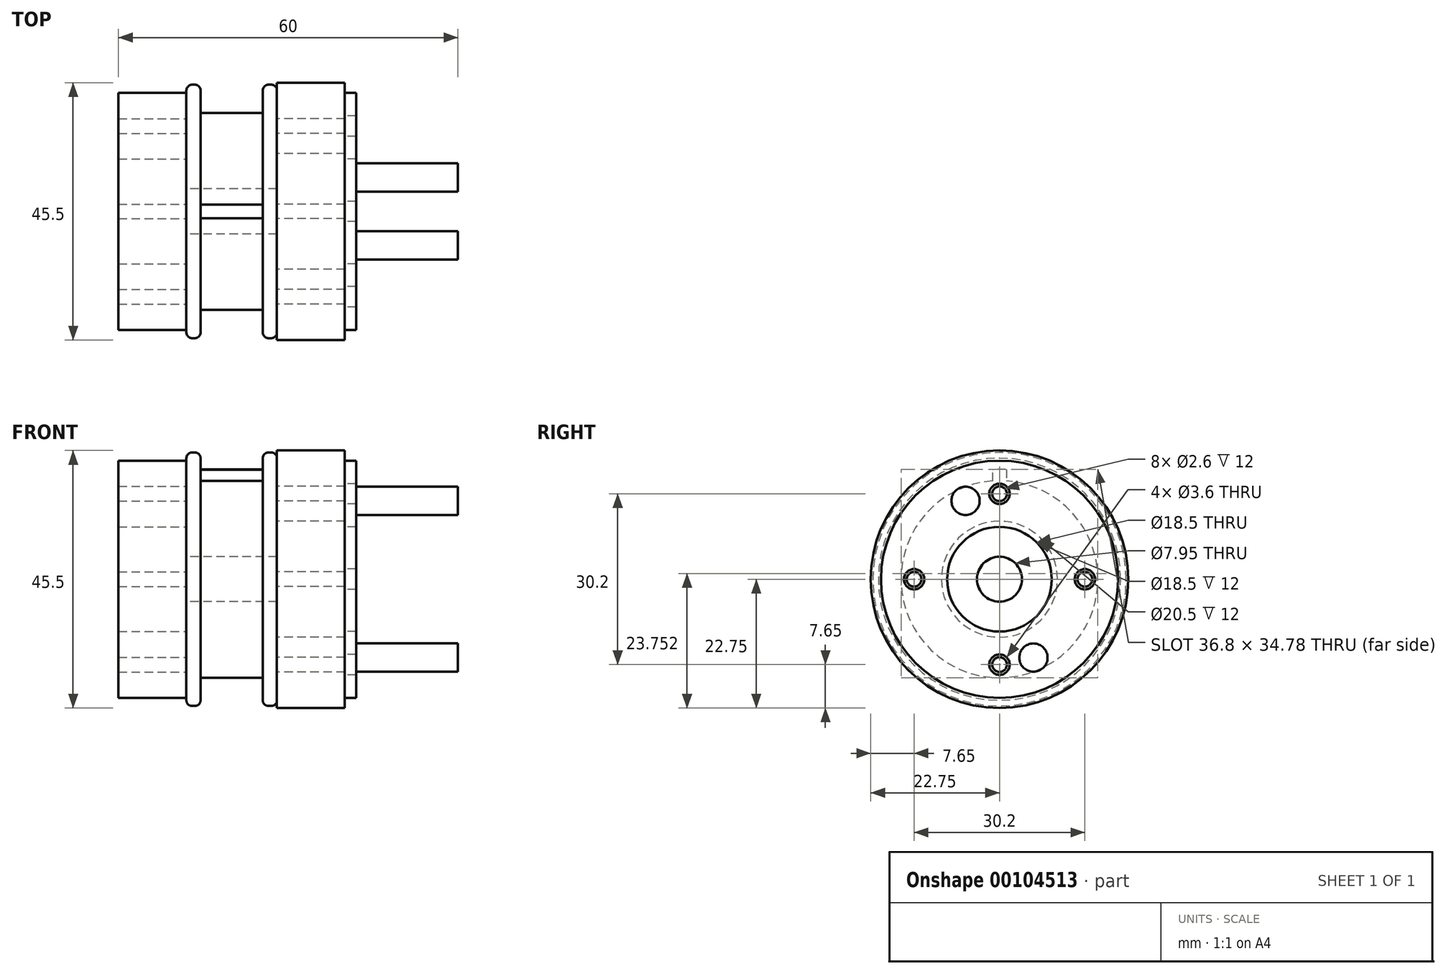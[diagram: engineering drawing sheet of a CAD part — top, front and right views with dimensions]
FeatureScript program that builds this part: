
annotation { "Feature Type Name" : "Feature", "Feature Type Description" : "" }
export const myFeature = defineFeature(function(context is Context, id is Id, definition is map)
    precondition{}
    {
        {
            var Q0;
            Q0=qCreatedBy(makeId("Right.planeOp"),FACE);
            var sketch = newSketch(context, id + "F0", { "sketchPlane" : qUnion([Q0])});
            skCircle(sketch, "E0", {"center": v(0, 0) * mm, "radius": 3.98 * mm});
            skCircle(sketch, "E1", {"center": v(0, 0) * mm, "radius": 14 * mm});
            skSolve(sketch);
        }
        {
            var Q0;
            Q0=makeQuery(id+"F0.imprint","IMPRINT",FACE,{"disambiguationData":[TD([[makeQuery(id+"F0.imprint","IMPRINT",EDGE,{"derivedFrom":sQuery(id+"F0.wireOp",EDGE,"E0")}),-1.0]])]});
            extrude(context, id + "F1", {"entities" : qUnion([Q0]), "endBound" : BoundingType.SYMMETRIC, "depth" : 16 * mm});
        }
        {
            var Q0;
            Q0=qCreatedBy(makeId("Right.planeOp"),FACE);
            var sketch = newSketch(context, id + "F2", { "sketchPlane" : qUnion([Q0])});
            skCircle(sketch, "E2", {"center": v(0, 0) * mm, "radius": 14 * mm});
            skCircle(sketch, "E3", {"center": v(0, 0) * mm, "radius": 17.4 * mm});
            skSolve(sketch);
        }
        {
            var Q0;
            Q0=makeQuery(id+"F2.imprint","IMPRINT",FACE,{"disambiguationData":[TD([[makeQuery(id+"F2.imprint","IMPRINT",EDGE,{"derivedFrom":sQuery(id+"F2.wireOp",EDGE,"E2")}),-1.0]])]});
            extrude(context, id + "F3", {"entities" : qUnion([Q0]), "operationType" : NewBodyOperationType.ADD, "endBound" : BoundingType.SYMMETRIC, "depth" : 16 * mm});
        }
        {
            var Q0;
            Q0=qCreatedBy(makeId("Front.planeOp"),FACE);
            var sketch = newSketch(context, id + "F4", { "sketchPlane" : qUnion([Q0])});
            skLineSegment(sketch, "E4", {"start": v(-27.37, 0) * mm, "end": v(29.66, 0) * mm});
            skLineSegment(sketch, "E5.bottom", {"start": v(-8, 22.4) * mm, "end": v(8, 22.4) * mm});
            skLineSegment(sketch, "E5.top", {"start": v(-8, 17.4) * mm, "end": v(8, 17.4) * mm});
            skLineSegment(sketch, "E5.left", {"start": v(-8, 22.4) * mm, "end": v(-8, 17.4) * mm});
            skLineSegment(sketch, "E5.right", {"start": v(8, 22.4) * mm, "end": v(8, 17.4) * mm});
            skLineSegment(sketch, "E6", {"start": v(-5.5, 22.4) * mm, "end": v(-5.5, 17.4) * mm});
            skLineSegment(sketch, "E7", {"start": v(5.5, 22.4) * mm, "end": v(5.5, 17.4) * mm});
            skSolve(sketch);
        }
        {
            var Q0;
            {var subQ0=sQuery(id+"F4.wireOp",EDGE,"E5.left");Q0=makeQuery(id+"F4.imprint","IMPRINT",FACE,{"disambiguationData":[TD([[makeQuery(id+"F4.imprint","IMPRINT",EDGE,{"derivedFrom":subQ0}),1.0]])]});}
            var Q1;
            {var subQ0=sQuery(id+"F4.wireOp",EDGE,"E5.right");Q1=makeQuery(id+"F4.imprint","IMPRINT",FACE,{"disambiguationData":[TD([[makeQuery(id+"F4.imprint","IMPRINT",EDGE,{"derivedFrom":subQ0}),-1.0]])]});}
            var Q2;
            Q2=sQuery(id+"F4.wireOp",EDGE,"E4");
            revolve(context, id + "F5", {"operationType" : NewBodyOperationType.ADD, "entities" : qUnion([Q0, Q1]), "axis" : qUnion([Q2]), "revolveType" : RevolveType.FULL});
        }
        {
            var Q0;
            {var subQ0=sQuery(id+"F4.wireOp",EDGE,"E6");Q0=makeQuery(id+"FOtlNRIKVtqWGdL_1.boolean.opBoolean","MERGE",FACE,{"derivedFrom":[makeQuery(id+"F5.opRevolve","SWEPT_FACE",FACE,{"disambiguationData":[OSD([subQ0])]}),makeQuery(id+"FOtlNRIKVtqWGdL_1.opRevolve","SWEPT_FACE",FACE,{"disambiguationData":[OSD([subQ0])]})]});}
            var sketch = newSketch(context, id + "F6", { "sketchPlane" : qUnion([Q0])});
            skArc(sketch, "E8", {"start": v(-1.2, 17.36) * mm, "mid": v(0, -17.4) * mm, "end": v(1.2, 17.36) * mm, "construction": true});
            skArc(sketch, "E9", {"start": v(1.2, 17.36) * mm, "mid": v(0, 17.4) * mm, "end": v(-1.2, 17.36) * mm});
            skPoint(sketch, "E10.visualSharp", {"position": v(-1.2, 19.37) * mm});
            skPoint(sketch, "E11.visualSharp", {"position": v(1.2, 19.37) * mm});
            skArc(sketch, "E12", {"start": v(-0.97, 19.38) * mm, "mid": v(0, -19.4) * mm, "end": v(0.98, 19.38) * mm});
            skArc(sketch, "E13", {"start": v(0.98, 19.38) * mm, "mid": v(-0.29, 19.4) * mm, "end": v(-1.55, 19.34) * mm});
            skLineSegment(sketch, "E14", {"start": v(-1.2, 17.36) * mm, "end": v(-1.2, 19.37) * mm});
            skLineSegment(sketch, "E15", {"start": v(1.2, 19.37) * mm, "end": v(1.2, 17.36) * mm});
            skSolve(sketch);
        }
        {
            var Q0;
            {var subQ0=sQuery(id+"F6.wireOp",EDGE,"E13");var subQ3=makeQuery(id+"F6.imprint","IMPRINT",VERTEX,{"derivedFrom":subQ0});Q0=makeQuery(id+"F6.imprint","IMPRINT",FACE,{"disambiguationData":[TD([[makeQuery(id+"F6.imprint","IMPRINT",EDGE,{"disambiguationData":[TD([[subQ3,1.0]])],"derivedFrom":subQ0}),1.0]])]});}
            var Q1;
            Q1=makeQuery(id+"F5.opRevolve","SWEPT_FACE",FACE,{"disambiguationData":[OSD([sQuery(id+"F4.wireOp",EDGE,"E7")])]});
            extrude(context, id + "F7", {"entities" : qUnion([Q0]), "operationType" : NewBodyOperationType.ADD, "endBound" : BoundingType.UP_TO_SURFACE, "endBoundEntityFace" : qUnion([Q1]), "depth" : 10 * mm});
        }
        {
            var Q0;
            Q0=makeQuery(id+"F5.opRevolve","SWEPT_EDGE",EDGE,{"disambiguationData":[OSD([sQuery(id+"F4.wireOp",EDGE,"E5.bottom"),sQuery(id+"F4.wireOp",EDGE,"E6")])]});
            var Q1;
            Q1=makeQuery(id+"F5.opRevolve","SWEPT_EDGE",EDGE,{"disambiguationData":[OSD([sQuery(id+"F4.wireOp",EDGE,"E5.bottom"),sQuery(id+"F4.wireOp",EDGE,"E7")])]});
            var Q2;
            Q2=makeQuery(id+"F5.opRevolve","SWEPT_EDGE",EDGE,{"disambiguationData":[OSD([sQuery(id+"F4.wireOp",EDGE,"E5.bottom"),sQuery(id+"F4.wireOp",EDGE,"E5.left")])]});
            var Q3;
            Q3=makeQuery(id+"F5.opRevolve","SWEPT_EDGE",EDGE,{"disambiguationData":[OSD([sQuery(id+"F4.wireOp",EDGE,"E5.bottom"),sQuery(id+"F4.wireOp",EDGE,"E5.right")])]});
            fillet(context, id + "F8", {"entities" : qUnion([Q0, Q1, Q2, Q3]), "radius" : 1 * mm, "tangentPropagation" : true, "allowEdgeOverflow" : false});
        }
        {
            var Q0;
            Q0=makeQuery(id+"F1.opExtrude","CAP_FACE",FACE,{"disambiguationData":[OSD([sQuery(id+"F0.wireOp",EDGE,"E0"),sQuery(id+"F0.wireOp",EDGE,"E1")])],"isStart":true});
            var sketch = newSketch(context, id + "F9", { "sketchPlane" : qUnion([Q0])});
            skCircle(sketch, "E16", {"center": v(0, 0) * mm, "radius": 9.25 * mm});
            skCircle(sketch, "E17", {"center": v(0, 0) * mm, "radius": 20.95 * mm});
            skCircle(sketch, "E18", {"center": v(0, 15.1) * mm, "radius": 1.3 * mm});
            skCircle(sketch, "E19", {"center": v(-15.1, 0) * mm, "radius": 1.3 * mm});
            skCircle(sketch, "E20", {"center": v(15.1, 0) * mm, "radius": 1.3 * mm});
            skCircle(sketch, "E21", {"center": v(0, -15.1) * mm, "radius": 1.3 * mm});
            skSolve(sketch);
        }
        {
            var Q0;
            Q0=makeQuery(id+"F9.imprint","IMPRINT",FACE,{"disambiguationData":[TD([[makeQuery(id+"F9.imprint","IMPRINT",EDGE,{"derivedFrom":sQuery(id+"F9.wireOp",EDGE,"E16")}),-1.0]])]});
            var Q1;
            Q1=makeQuery(id+"F9.imprint","IMPRINT",FACE,{"disambiguationData":[TD([[makeQuery(id+"F9.imprint","IMPRINT",EDGE,{"derivedFrom":sQuery(id+"F9.wireOp",EDGE,"E17")}),1.0]])]});
            extrude(context, id + "F10", {"entities" : qUnion([Q0, Q1]), "operationType" : NewBodyOperationType.ADD, "depth" : 12 * mm});
        }
        {
            var Q0;
            Q0=makeQuery(id+"F5.boolean.opBoolean","MERGE",FACE,{"derivedFrom":[makeQuery(id+"F3.boolean.opBoolean","MERGE",FACE,{"derivedFrom":[makeQuery(id+"F1.opExtrude","CAP_FACE",FACE,{"disambiguationData":[OSD([sQuery(id+"F0.wireOp",EDGE,"E0"),sQuery(id+"F0.wireOp",EDGE,"E1")])],"isStart":false}),makeQuery(id+"F3.opExtrude","CAP_FACE",FACE,{"disambiguationData":[OSD([sQuery(id+"F2.wireOp",EDGE,"E2"),sQuery(id+"F2.wireOp",EDGE,"E3")])],"isStart":false})]}),makeQuery(id+"F5.opRevolve","SWEPT_FACE",FACE,{"disambiguationData":[OSD([sQuery(id+"F4.wireOp",EDGE,"E5.right")])]})]});
            var sketch = newSketch(context, id + "F11", { "sketchPlane" : qUnion([Q0])});
            skCircle(sketch, "E22", {"center": v(0, 0) * mm, "radius": 22.75 * mm});
            skCircle(sketch, "E23", {"center": v(0, 0) * mm, "radius": 10.25 * mm});
            skCircle(sketch, "E24", {"center": v(0, 15.1) * mm, "radius": 1.3 * mm});
            skCircle(sketch, "E25", {"center": v(-15.1, 0) * mm, "radius": 1.3 * mm});
            skCircle(sketch, "E26", {"center": v(0, -15.1) * mm, "radius": 1.3 * mm});
            skCircle(sketch, "E27", {"center": v(15.1, 0) * mm, "radius": 1.3 * mm});
            skSolve(sketch);
        }
        {
            var Q0;
            Q0=makeQuery(id+"F11.imprint","IMPRINT",FACE,{"disambiguationData":[TD([[makeQuery(id+"F11.imprint","IMPRINT",EDGE,{"derivedFrom":sQuery(id+"F11.wireOp",EDGE,"E22")}),1.0]])]});
            var Q1;
            Q1=makeQuery(id+"F11.imprint","IMPRINT",FACE,{"disambiguationData":[TD([[makeQuery(id+"F11.imprint","IMPRINT",EDGE,{"derivedFrom":sQuery(id+"F11.wireOp",EDGE,"E23")}),-1.0]])]});
            extrude(context, id + "F12", {"entities" : qUnion([Q0, Q1]), "operationType" : NewBodyOperationType.ADD, "depth" : 12 * mm});
        }
        {
            var Q0;
            Q0=makeQuery(id+"F12.opExtrude","CAP_FACE",FACE,{"disambiguationData":[OSD([sQuery(id+"F11.wireOp",EDGE,"E22"),sQuery(id+"F11.wireOp",EDGE,"E23"),sQuery(id+"F11.wireOp",EDGE,"E24"),sQuery(id+"F11.wireOp",EDGE,"E25"),sQuery(id+"F11.wireOp",EDGE,"E26"),sQuery(id+"F11.wireOp",EDGE,"E27")])],"isStart":false});
            var sketch = newSketch(context, id + "F13", { "sketchPlane" : qUnion([Q0])});
            skCircle(sketch, "E28", {"center": v(0, 0) * mm, "radius": 9.25 * mm});
            skCircle(sketch, "E29", {"center": v(0, 0) * mm, "radius": 20.95 * mm});
            skCircle(sketch, "E30", {"center": v(0, 15.1) * mm, "radius": 1.8 * mm});
            skCircle(sketch, "E31", {"center": v(-15.1, 0) * mm, "radius": 1.8 * mm});
            skCircle(sketch, "E32", {"center": v(0, -15.1) * mm, "radius": 1.8 * mm});
            skCircle(sketch, "E33", {"center": v(15.1, 0) * mm, "radius": 1.8 * mm});
            skSolve(sketch);
        }
        {
            var Q0;
            Q0=makeQuery(id+"F13.imprint","IMPRINT",FACE,{"disambiguationData":[TD([[makeQuery(id+"F13.imprint","IMPRINT",EDGE,{"derivedFrom":sQuery(id+"F13.wireOp",EDGE,"E28")}),-1.0]])]});
            var Q1;
            Q1=makeQuery(id+"F13.imprint","IMPRINT",FACE,{"disambiguationData":[TD([[makeQuery(id+"F13.imprint","IMPRINT",EDGE,{"derivedFrom":sQuery(id+"F13.wireOp",EDGE,"E29")}),1.0]])]});
            extrude(context, id + "F14", {"entities" : qUnion([Q0, Q1]), "depth" : 2 * mm});
        }
        {
            var Q0;
            Q0=makeQuery(id+"F14.opExtrude","CAP_FACE",FACE,{"disambiguationData":[OSD([sQuery(id+"F13.wireOp",EDGE,"E28"),sQuery(id+"F13.wireOp",EDGE,"E29"),sQuery(id+"F13.wireOp",EDGE,"E30"),sQuery(id+"F13.wireOp",EDGE,"E31"),sQuery(id+"F13.wireOp",EDGE,"E32"),sQuery(id+"F13.wireOp",EDGE,"E33")])],"isStart":false});
            var sketch = newSketch(context, id + "F15", { "sketchPlane" : qUnion([Q0])});
            skCircle(sketch, "E34", {"center": v(-6, 13.86) * mm, "radius": 2.5 * mm});
            skCircle(sketch, "E35", {"center": v(6, -13.86) * mm, "radius": 2.5 * mm});
            skSolve(sketch);
        }
        {
            var Q0;
            Q0=makeQuery(id+"F15.imprint","IMPRINT",FACE,{"disambiguationData":[TD([[makeQuery(id+"F15.imprint","IMPRINT",EDGE,{"derivedFrom":sQuery(id+"F15.wireOp",EDGE,"E34")}),1.0]])]});
            var Q1;
            Q1=makeQuery(id+"F15.imprint","IMPRINT",FACE,{"disambiguationData":[TD([[makeQuery(id+"F15.imprint","IMPRINT",EDGE,{"derivedFrom":sQuery(id+"F15.wireOp",EDGE,"E35")}),1.0]])]});
            extrude(context, id + "F16", {"entities" : qUnion([Q0, Q1]), "operationType" : NewBodyOperationType.ADD, "depth" : 18 * mm});
        }
    });
